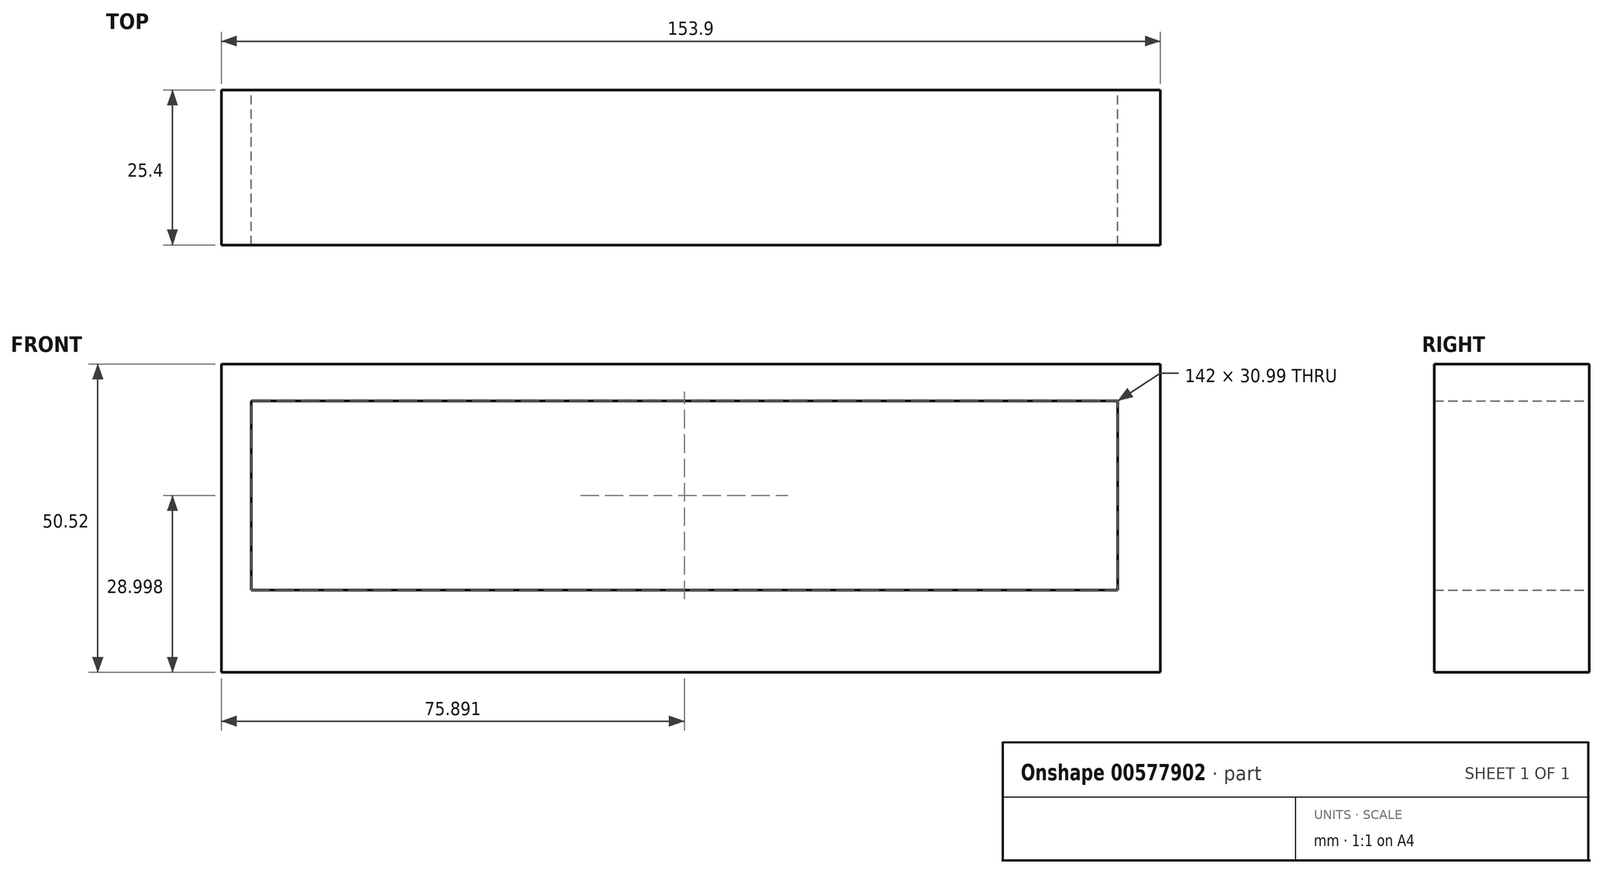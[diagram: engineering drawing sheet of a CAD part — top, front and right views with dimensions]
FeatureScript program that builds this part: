
annotation { "Feature Type Name" : "Feature", "Feature Type Description" : "" }
export const myFeature = defineFeature(function(context is Context, id is Id, definition is map)
    precondition{}
    {
        {
            var Q0;
            Q0=qCreatedBy(makeId("Front.planeOp"),FACE);
            var sketch = newSketch(context, id + "F0", { "sketchPlane" : qUnion([Q0])});
            skLineSegment(sketch, "E0", {"start": v(-76.13, 50.52) * mm, "end": v(-76.13, 0) * mm});
            skLineSegment(sketch, "E1", {"start": v(-76.13, 0) * mm, "end": v(77.77, 0) * mm});
            skLineSegment(sketch, "E2", {"start": v(77.77, 0) * mm, "end": v(77.77, 50.52) * mm});
            skLineSegment(sketch, "E3", {"start": v(77.77, 50.52) * mm, "end": v(-76.13, 50.52) * mm});
            skSolve(sketch);
        }
        {
            var Q0;
            Q0=qCreatedBy(makeId("Front.planeOp"),FACE);
            var sketch = newSketch(context, id + "F1", { "sketchPlane" : qUnion([Q0])});
            skLineSegment(sketch, "E4.bottom", {"start": v(-71.24, 44.5) * mm, "end": v(70.76, 44.5) * mm});
            skLineSegment(sketch, "E4.top", {"start": v(-71.24, 13.5) * mm, "end": v(70.76, 13.5) * mm});
            skLineSegment(sketch, "E4.left", {"start": v(-71.24, 44.5) * mm, "end": v(-71.24, 13.5) * mm});
            skLineSegment(sketch, "E4.right", {"start": v(70.76, 44.5) * mm, "end": v(70.76, 13.5) * mm});
            skSolve(sketch);
        }
        {
            var Q0;
            Q0=makeQuery(id+"F0.imprint","IMPRINT",FACE,{"disambiguationData":[TD([[makeQuery(id+"F0.imprint","IMPRINT",EDGE,{"derivedFrom":sQuery(id+"F0.wireOp",EDGE,"E0")}),1.0]])]});
            extrude(context, id + "F2", {"entities" : qUnion([Q0]), "depth" : 25.4 * mm, "offsetDistance" : 25.4 * mm});
        }
        {
            var Q0;
            Q0=makeQuery(id+"F1.imprint","IMPRINT",FACE,{"disambiguationData":[TD([[makeQuery(id+"F1.imprint","IMPRINT",EDGE,{"derivedFrom":sQuery(id+"F1.wireOp",EDGE,"E4.bottom")}),-1.0]])]});
            extrude(context, id + "F3", {"entities" : qUnion([Q0]), "operationType" : NewBodyOperationType.REMOVE, "depth" : 71.4 * mm, "offsetDistance" : 25.4 * mm});
        }
    });
